# Revit family: ARKOSLIGHT_GAP Black Foster Micro Custom Cover
name_source: partatom
category: Lighting Fixtures
units: mm (PartAtom-declared; Revit-internal decimal feet)

## family parameters
Cut with Voids When Loaded = No
Host = Face
Light Source = No
Part Type = Normal
Room Calculation Point = No
Round Connector Dimension = Use Diameter
Shared = No

## types (1)
- A450000XN - BLACK FOSTER MICRO CUSTOM COVER GAP X N
    ARKOSLIGHT_Body Color = ARKOSLIGHT_Matt black
    ARKOSLIGHT_Color = Black
    ARKOSLIGHT_Fixture Type = ACCESSORIES
    ARKOSLIGHT_Model = BLACK FOSTER CUSTOM ACCESSORIES
    ARKOSLIGHT_Reference = A450000XN
    ARKOSLIGHT_Series = BLACK FOSTER MICRO CUSTOM SURFACE ACCESSORIES
    Apparent Load = 0 VA
    Default Elevation = 0 mm  [stored 0 ft]
    Description = Select the number and length of profiles suitable for the defined length.
    Manufacturer = ARKOSLIGHT
    Model = BLACK FOSTER CUSTOM ACCESSORIES
    URL = https://www.arkoslight.com

note: [stored X ft] marks values corroborated as IEEE doubles in the binary element streams (Revit-internal decimal feet)

## geometry (parser evidence)
native form markers: Sweep x2
no freeform markers — native parametric forms only
